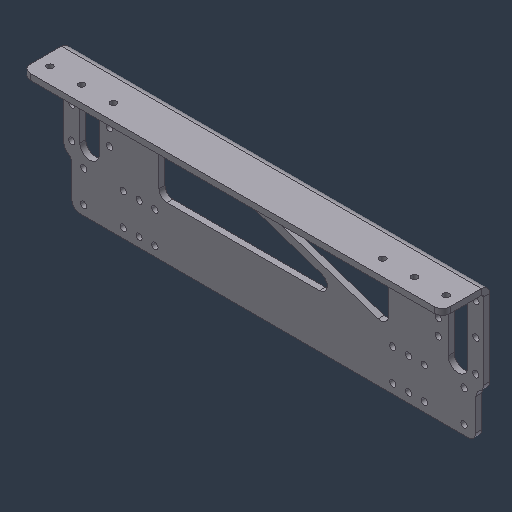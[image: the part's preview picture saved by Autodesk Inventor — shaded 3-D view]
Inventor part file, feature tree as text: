
AUTODESK INVENTOR PART (.ipt)
format: ipt  version: 2024.3 (Build 283343000, 343)  size: 352,768 bytes
history: native  units: mm (DEFAULTED — no unit token found)
features: sketch x7, sheet_metal_op x4, hole x4, other x4, pattern_linear x3, mirror x2, chamfer x1
ambient origin geometry x8: Origin, YZ Plane, XZ Plane, XY Plane, X Axis, Y Axis, Z Axis, Center Point
bodies: Solid1 (feature_tree)
feature tree (25):
  sheet_metal_op  "Face1"
  sheet_metal_op  "Flange1"
  hole  "Hole1"  [1 undecoded]
  hole  "Hole2"  [1 undecoded]
  pattern_linear  "Rectangular Pattern1"  Spacing1=4.7625mm  [1 undecoded]
  pattern_linear  "Rectangular Pattern2"  Spacing1=7.14375mm  [1 undecoded]
  hole  "Hole3"  [1 undecoded]
  sketch  "Sketch8"  dims[d10=19.05mm d11=4.7625mm d12=7.14375mm d13=323.85mm d14=50.8mm d15=5.1054mm d16=9.652mm d17=9.779mm d18=1.9558mm d19=14.3117mm d20=4.7625mm d21=20.594885mm d22=63.5mm d23=190.5mm d24=3.175mm d25=3.175mm d26=4.7625mm d27=0.0mm d29=7.9375mm d30=44.45mm d31=147.6375mm d44=12.7mm d45=39.6875mm d46=25.4mm d47=47.625mm d48=5.1054mm d49=19.05mm d50=9.525mm d51=6.35mm d52=14.3117mm d53=25.4mm d54=20.594885mm d55=20.0mm d57=31.75mm d58=19.05mm d59=30.0mm d61=12.7mm d62=25.4mm d63=7.9375mm d64=19.1516mm d65=5.1054mm d66=9.652mm d67=9.779mm d68=6.35mm d69=14.3117mm d70=4.7625mm d71=20.594885mm d72=20.6375mm d73=9.525mm d74=5.1054mm d75=9.652mm d76=9.525mm d77=6.35mm d78=14.3117mm d79=4.7625mm d80=20.594885mm d81=30.0mm d83=25.4mm d85=38.1mm d86=6.35mm d87=6.35mm d88=6.35mm d89=6.35mm]
  mirror  "Mirror1"
  hole  "Hole4"  [1 undecoded]
  pattern_linear  "Rectangular Pattern3"  Spacing1=20.594885mm  [1 undecoded]
  mirror  "Mirror2"
  chamfer  "Corner Round3"
  sketch  "Sketch1"  dims[d0=336.55mm d1=103.9368mm]
  other  "Plate1"
  sketch  "Sketch2"  dims[d2=4.7625mm d3=4.7625mm]
  other  "Plate2"
  sheet_metal_op  "Bend1"
  sheet_metal_op  "Corner1"
  sketch  "Sketch3"  dims[d4=2.38125mm]
  sketch  "Sketch4"  dims[d5=9.525mm]
  sketch  "Sketch6"  dims[d6=7.14375mm]
  sketch  "Sketch7"  dims[d7=38.1mm d8=90.0deg d9=2.0mm]
  other  "Cut1"
  other  "Definition1"
note: 7 required parameter values undecoded (feature->parameter linkage not recoverable at this tier; creation-order binding heuristic only, values carry confidence <= 0.55)
